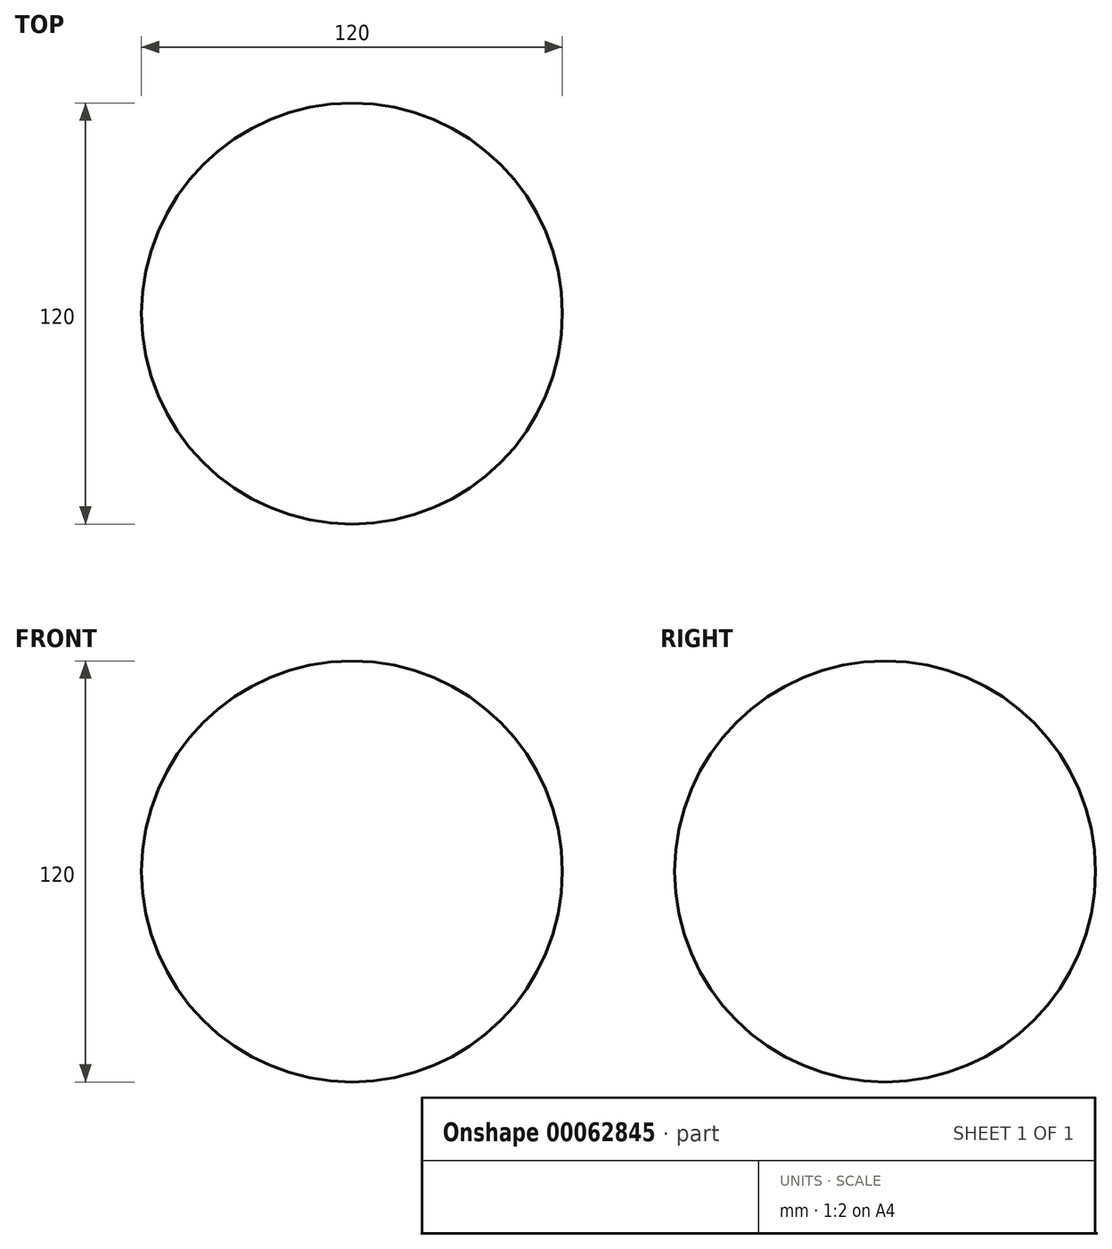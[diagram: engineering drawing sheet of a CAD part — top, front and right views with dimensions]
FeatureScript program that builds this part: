
annotation { "Feature Type Name" : "Feature", "Feature Type Description" : "" }
export const myFeature = defineFeature(function(context is Context, id is Id, definition is map)
    precondition{}
    {
        {
            var Q0;
            Q0=qCreatedBy(makeId("Front.planeOp"),FACE);
            var sketch = newSketch(context, id + "F0", { "sketchPlane" : qUnion([Q0])});
            skArc(sketch, "E0", {"start": v(0, -60) * mm, "mid": v(60, 0) * mm, "end": v(0, 60) * mm});
            skLineSegment(sketch, "E1", {"start": v(0, 60) * mm, "end": v(0, -60) * mm});
            skSolve(sketch);
        }
        {
            var Q0;
            Q0 = qSketchRegion(id + "F0", true);
            var Q1;
            Q1=sQuery(id+"F0.wireOp",EDGE,"E1");
            revolve(context, id + "F1", {"entities" : qUnion([Q0]), "axis" : qUnion([Q1]), "revolveType" : RevolveType.FULL});
        }
    });
